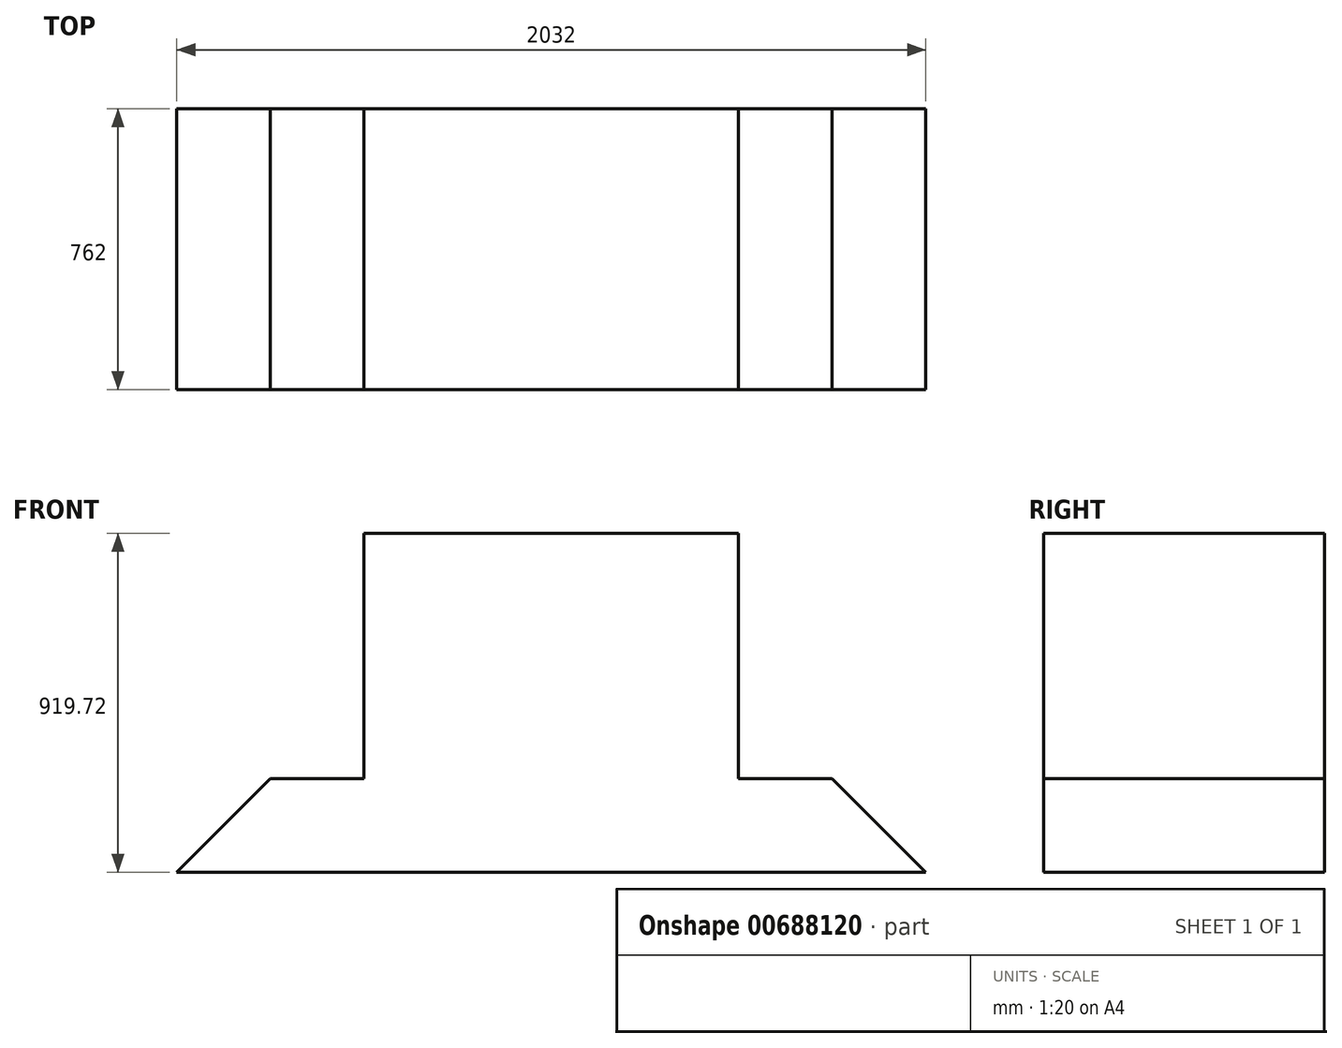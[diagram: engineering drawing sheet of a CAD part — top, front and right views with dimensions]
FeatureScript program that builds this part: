
annotation { "Feature Type Name" : "Feature", "Feature Type Description" : "" }
export const myFeature = defineFeature(function(context is Context, id is Id, definition is map)
    precondition{}
    {
        {
            var Q0;
            Q0=qCreatedBy(makeId("Front.planeOp"),FACE);
            var sketch = newSketch(context, id + "F0", { "sketchPlane" : qUnion([Q0])});
            skLineSegment(sketch, "E0", {"start": v(0, 0) * mm, "end": v(2032, 0) * mm});
            skLineSegment(sketch, "E1", {"start": v(2032, 0) * mm, "end": v(1778, 254) * mm});
            skLineSegment(sketch, "E2", {"start": v(1778, 254) * mm, "end": v(1524, 254) * mm});
            skLineSegment(sketch, "E3", {"start": v(1524, 254) * mm, "end": v(1524, 919.72) * mm});
            skLineSegment(sketch, "E4", {"start": v(1524, 919.72) * mm, "end": v(508, 919.72) * mm});
            skLineSegment(sketch, "E5", {"start": v(508, 919.72) * mm, "end": v(508, 254) * mm});
            skLineSegment(sketch, "E6", {"start": v(508, 254) * mm, "end": v(254, 254) * mm});
            skLineSegment(sketch, "E7", {"start": v(254, 254) * mm, "end": v(0, 0) * mm});
            skSolve(sketch);
        }
        {
            var Q0;
            Q0=makeQuery(id+"F0.imprint","IMPRINT",FACE,{"disambiguationData":[TD([[makeQuery(id+"F0.imprint","IMPRINT",EDGE,{"derivedFrom":sQuery(id+"F0.wireOp",EDGE,"E0")}),1.0]])]});
            extrude(context, id + "F1", {"entities" : qUnion([Q0]), "depth" : 762 * mm, "offsetDistance" : 25.4 * mm});
        }
    });
